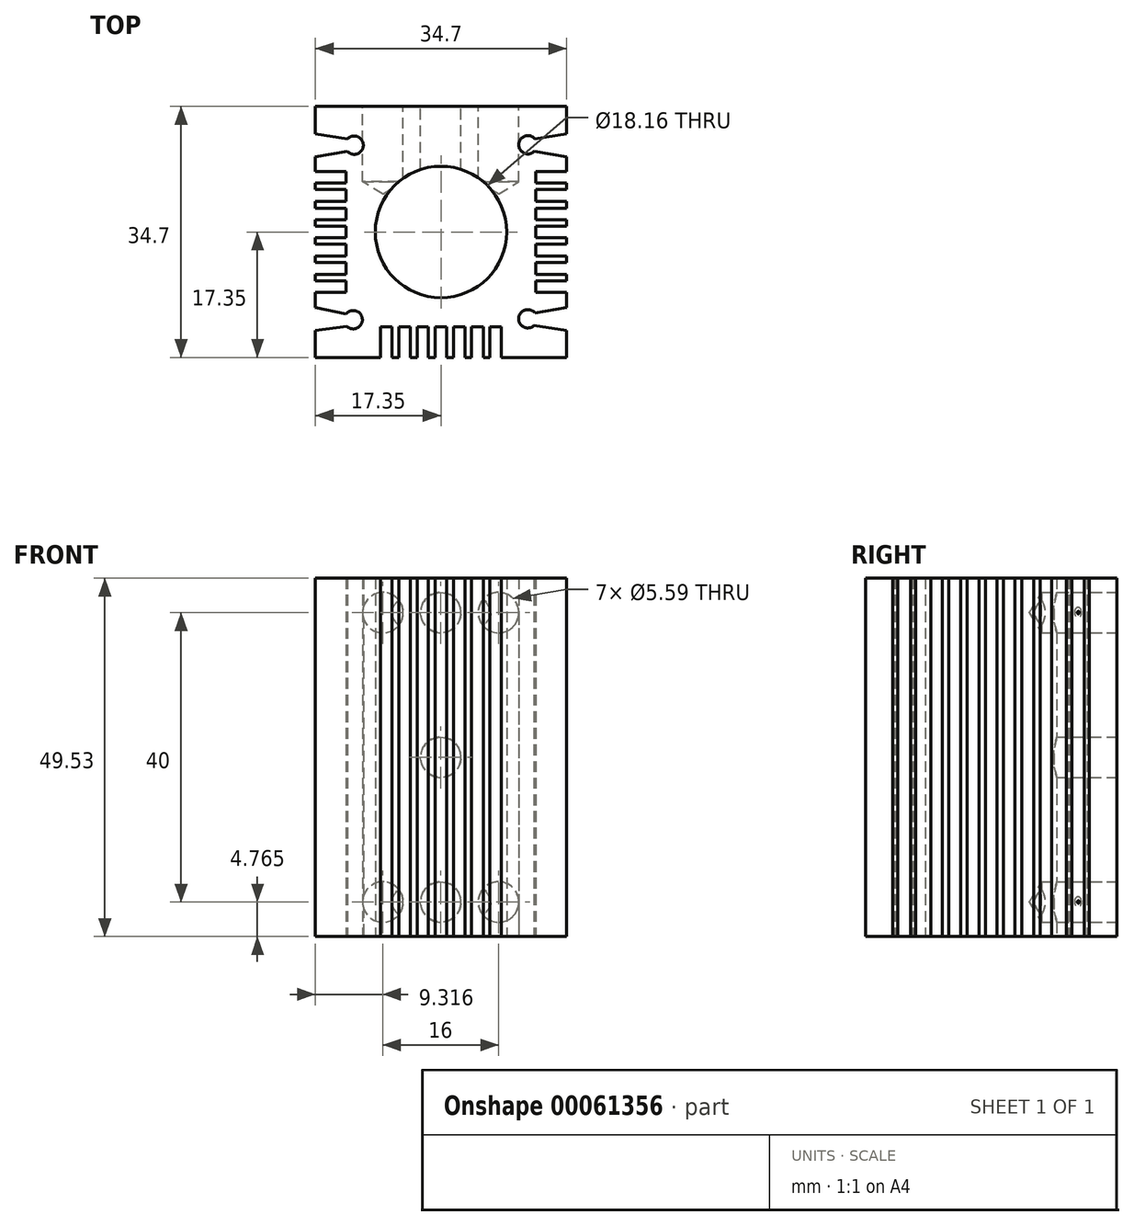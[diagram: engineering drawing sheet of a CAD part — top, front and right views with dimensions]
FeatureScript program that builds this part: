
annotation { "Feature Type Name" : "Feature", "Feature Type Description" : "" }
export const myFeature = defineFeature(function(context is Context, id is Id, definition is map)
    precondition{}
    {
        {
            var Q0;
            Q0=qCreatedBy(makeId("Top.planeOp"),FACE);
            var sketch = newSketch(context, id + "F0", { "sketchPlane" : qUnion([Q0])});
            skLineSegment(sketch, "E0.rect.top", {"start": v(-17.35, -17.35) * mm, "end": v(-8.36, -17.35) * mm});
            skLineSegment(sketch, "E0.rect.left", {"start": v(-17.35, 17.35) * mm, "end": v(-17.35, 13.59) * mm});
            skLineSegment(sketch, "E0.rect.right", {"start": v(17.35, 17.35) * mm, "end": v(17.35, 13.59) * mm});
            skPoint(sketch, "E0.rect.middle", {"position": v(0, 0) * mm});
            skLineSegment(sketch, "E1.rect.left", {"start": v(-6.76, -17.35) * mm, "end": v(-6.76, -13.13) * mm});
            skLineSegment(sketch, "E1.rect.right", {"start": v(6.76, -17.35) * mm, "end": v(6.76, -13.13) * mm});
            skLineSegment(sketch, "E2.rect.left", {"start": v(-5.84, -17.35) * mm, "end": v(-5.84, -13.13) * mm});
            skLineSegment(sketch, "E2.rect.right", {"start": v(5.84, -17.35) * mm, "end": v(5.84, -13.13) * mm});
            skLineSegment(sketch, "E3.trimOffspring", {"start": v(-8.36, -13.13) * mm, "end": v(-8.36, -17.35) * mm});
            skLineSegment(sketch, "E4.trimOffspring", {"start": v(-4.24, -13.13) * mm, "end": v(-4.24, -17.35) * mm});
            skLineSegment(sketch, "E5.trimOffspring", {"start": v(-3.3, -13.13) * mm, "end": v(-3.3, -17.35) * mm});
            skLineSegment(sketch, "E6.trimOffspring", {"start": v(-1.74, -13.13) * mm, "end": v(-1.74, -17.35) * mm});
            skLineSegment(sketch, "E7.trimOffspring", {"start": v(-0.79, -13.13) * mm, "end": v(-0.79, -17.35) * mm});
            skLineSegment(sketch, "E8.trimOffspring", {"start": v(0.79, -13.13) * mm, "end": v(0.79, -17.35) * mm});
            skLineSegment(sketch, "E9.trimOffspring", {"start": v(1.74, -13.13) * mm, "end": v(1.74, -17.35) * mm});
            skLineSegment(sketch, "E10.trimOffspring", {"start": v(3.3, -13.13) * mm, "end": v(3.3, -17.35) * mm});
            skLineSegment(sketch, "E11.trimOffspring", {"start": v(4.24, -13.13) * mm, "end": v(4.24, -17.35) * mm});
            skLineSegment(sketch, "E12.trimOffspring", {"start": v(8.36, -13.13) * mm, "end": v(8.36, -17.35) * mm});
            skLineSegment(sketch, "E13.trimOffspring", {"start": v(-6.76, -17.35) * mm, "end": v(-5.84, -17.35) * mm});
            skLineSegment(sketch, "E14.trimOffspring", {"start": v(-4.24, -17.35) * mm, "end": v(-3.3, -17.35) * mm});
            skLineSegment(sketch, "E15.trimOffspring", {"start": v(-1.74, -17.35) * mm, "end": v(-0.79, -17.35) * mm});
            skLineSegment(sketch, "E16.trimOffspring", {"start": v(0.79, -17.35) * mm, "end": v(1.74, -17.35) * mm});
            skLineSegment(sketch, "E17.trimOffspring", {"start": v(3.3, -17.35) * mm, "end": v(4.24, -17.35) * mm});
            skLineSegment(sketch, "E18.trimOffspring", {"start": v(5.84, -17.35) * mm, "end": v(6.76, -17.35) * mm});
            skLineSegment(sketch, "E19.trimOffspring", {"start": v(8.36, -17.35) * mm, "end": v(17.35, -17.35) * mm});
            skLineSegment(sketch, "E20.trimOffspring", {"start": v(-8.36, -13.13) * mm, "end": v(-6.76, -13.13) * mm});
            skLineSegment(sketch, "E21.trimOffspring", {"start": v(-5.84, -13.13) * mm, "end": v(-4.24, -13.13) * mm});
            skLineSegment(sketch, "E22.trimOffspring", {"start": v(-3.3, -13.13) * mm, "end": v(-1.74, -13.13) * mm});
            skLineSegment(sketch, "E23.trimOffspring", {"start": v(-0.79, -13.13) * mm, "end": v(0.79, -13.13) * mm});
            skLineSegment(sketch, "E24.trimOffspring", {"start": v(1.74, -13.13) * mm, "end": v(3.3, -13.13) * mm});
            skLineSegment(sketch, "E25.trimOffspring", {"start": v(4.24, -13.13) * mm, "end": v(5.84, -13.13) * mm});
            skLineSegment(sketch, "E26.trimOffspring", {"start": v(6.76, -13.13) * mm, "end": v(8.36, -13.13) * mm});
            skPoint(sketch, "E27.rect.right.end.orphan", {"position": v(23.47, -13.13) * mm});
            skPoint(sketch, "E27.rect.left.end.orphan", {"position": v(-23.47, -13.13) * mm});
            skPoint(sketch, "E28.trimOffspring.end.orphan", {"position": v(23.47, 13.13) * mm});
            skPoint(sketch, "E27.rect.bottom.start.orphan", {"position": v(-23.47, 13.13) * mm});
            skLineSegment(sketch, "E29.rect.bottom", {"start": v(-17.35, 5.86) * mm, "end": v(-13.13, 5.86) * mm});
            skLineSegment(sketch, "E29.rect.top", {"start": v(-17.35, -5.86) * mm, "end": v(-13.13, -5.86) * mm});
            skLineSegment(sketch, "E30.rect.bottom", {"start": v(17.35, -6.78) * mm, "end": v(13.13, -6.78) * mm});
            skLineSegment(sketch, "E30.rect.top", {"start": v(17.35, 6.78) * mm, "end": v(13.13, 6.78) * mm});
            skLineSegment(sketch, "E31.rect.bottom", {"start": v(17.35, -8.36) * mm, "end": v(13.13, -8.36) * mm});
            skLineSegment(sketch, "E31.rect.top", {"start": v(17.35, 8.36) * mm, "end": v(13.13, 8.36) * mm});
            skLineSegment(sketch, "E32.rect.left", {"start": v(13.13, 8.36) * mm, "end": v(13.13, 6.78) * mm});
            skLineSegment(sketch, "E33.trimOffspring", {"start": v(-13.13, 8.36) * mm, "end": v(-17.35, 8.36) * mm});
            skLineSegment(sketch, "E34.trimOffspring", {"start": v(-13.13, 6.78) * mm, "end": v(-17.35, 6.78) * mm});
            skLineSegment(sketch, "E35.trimOffspring", {"start": v(13.13, 5.86) * mm, "end": v(17.35, 5.86) * mm});
            skLineSegment(sketch, "E36.trimOffspring", {"start": v(13.13, 4.22) * mm, "end": v(17.35, 4.22) * mm});
            skLineSegment(sketch, "E37.trimOffspring", {"start": v(13.13, 3.3) * mm, "end": v(17.35, 3.3) * mm});
            skLineSegment(sketch, "E38.trimOffspring", {"start": v(13.13, 1.68) * mm, "end": v(17.35, 1.68) * mm});
            skLineSegment(sketch, "E39.trimOffspring", {"start": v(13.13, 0.79) * mm, "end": v(17.35, 0.79) * mm});
            skLineSegment(sketch, "E40.trimOffspring", {"start": v(13.13, -0.79) * mm, "end": v(17.35, -0.79) * mm});
            skLineSegment(sketch, "E41.trimOffspring", {"start": v(13.13, -1.68) * mm, "end": v(17.35, -1.68) * mm});
            skLineSegment(sketch, "E42.trimOffspring", {"start": v(13.13, -3.3) * mm, "end": v(17.35, -3.3) * mm});
            skLineSegment(sketch, "E43.trimOffspring", {"start": v(13.13, -4.22) * mm, "end": v(17.35, -4.22) * mm});
            skLineSegment(sketch, "E44.trimOffspring", {"start": v(13.13, -5.86) * mm, "end": v(17.35, -5.86) * mm});
            skLineSegment(sketch, "E45.trimOffspring", {"start": v(-13.13, -6.78) * mm, "end": v(-17.35, -6.78) * mm});
            skLineSegment(sketch, "E46.trimOffspring", {"start": v(-13.13, -8.36) * mm, "end": v(-17.35, -8.36) * mm});
            skLineSegment(sketch, "E47.trimOffspring", {"start": v(-17.35, 4.22) * mm, "end": v(-13.13, 4.22) * mm});
            skLineSegment(sketch, "E48.trimOffspring", {"start": v(-17.35, 3.3) * mm, "end": v(-13.13, 3.3) * mm});
            skLineSegment(sketch, "E49.trimOffspring", {"start": v(-17.35, 1.68) * mm, "end": v(-13.13, 1.68) * mm});
            skLineSegment(sketch, "E50.trimOffspring", {"start": v(-17.35, 0.79) * mm, "end": v(-13.13, 0.79) * mm});
            skLineSegment(sketch, "E51.trimOffspring", {"start": v(-17.35, -0.79) * mm, "end": v(-13.13, -0.79) * mm});
            skLineSegment(sketch, "E52.trimOffspring", {"start": v(-17.35, -1.68) * mm, "end": v(-13.13, -1.68) * mm});
            skLineSegment(sketch, "E53.trimOffspring", {"start": v(-17.35, -3.3) * mm, "end": v(-13.13, -3.3) * mm});
            skLineSegment(sketch, "E54.trimOffspring", {"start": v(-17.35, -4.22) * mm, "end": v(-13.13, -4.22) * mm});
            skPoint(sketch, "E32.rect.top.end.orphan", {"position": v(-13.13, -20.84) * mm});
            skPoint(sketch, "E32.rect.top.start.orphan", {"position": v(13.13, -20.84) * mm});
            skPoint(sketch, "E55.orphan", {"position": v(13.13, 20.84) * mm});
            skLineSegment(sketch, "E56.trimOffspring", {"start": v(-13.13, 8.36) * mm, "end": v(-13.13, 6.78) * mm});
            skPoint(sketch, "E32.rect.right.start.orphan", {"position": v(-13.13, 20.84) * mm});
            skLineSegment(sketch, "E57.trimOffspring", {"start": v(-17.35, -8.36) * mm, "end": v(-17.35, -10.46) * mm});
            skLineSegment(sketch, "E58.trimOffspring", {"start": v(-17.35, -5.86) * mm, "end": v(-17.35, -6.78) * mm});
            skLineSegment(sketch, "E59.trimOffspring", {"start": v(-17.35, -3.3) * mm, "end": v(-17.35, -4.22) * mm});
            skLineSegment(sketch, "E60.trimOffspring", {"start": v(-17.35, -0.79) * mm, "end": v(-17.35, -1.68) * mm});
            skLineSegment(sketch, "E61.trimOffspring", {"start": v(-17.35, 1.68) * mm, "end": v(-17.35, 0.79) * mm});
            skLineSegment(sketch, "E62.trimOffspring", {"start": v(-17.35, 4.22) * mm, "end": v(-17.35, 3.3) * mm});
            skLineSegment(sketch, "E63.trimOffspring", {"start": v(-17.35, 6.78) * mm, "end": v(-17.35, 5.86) * mm});
            skLineSegment(sketch, "E64.trimOffspring", {"start": v(-13.13, 5.86) * mm, "end": v(-13.13, 4.22) * mm});
            skLineSegment(sketch, "E65.trimOffspring", {"start": v(-13.13, 3.3) * mm, "end": v(-13.13, 1.68) * mm});
            skLineSegment(sketch, "E66.trimOffspring", {"start": v(-13.13, 0.79) * mm, "end": v(-13.13, -0.79) * mm});
            skLineSegment(sketch, "E67.trimOffspring", {"start": v(-13.13, -1.68) * mm, "end": v(-13.13, -3.3) * mm});
            skLineSegment(sketch, "E68.trimOffspring", {"start": v(-13.13, -4.22) * mm, "end": v(-13.13, -5.86) * mm});
            skLineSegment(sketch, "E69.trimOffspring", {"start": v(-13.13, -6.78) * mm, "end": v(-13.13, -8.36) * mm});
            skLineSegment(sketch, "E70", {"start": v(13.13, -8.36) * mm, "end": v(13.13, -6.78) * mm});
            skLineSegment(sketch, "E71.trimOffspring", {"start": v(17.35, -8.36) * mm, "end": v(17.35, -10.46) * mm});
            skLineSegment(sketch, "E72.trimOffspring", {"start": v(17.35, -5.86) * mm, "end": v(17.35, -6.78) * mm});
            skLineSegment(sketch, "E73.trimOffspring", {"start": v(17.35, -3.3) * mm, "end": v(17.35, -4.22) * mm});
            skLineSegment(sketch, "E74.trimOffspring", {"start": v(17.35, -0.79) * mm, "end": v(17.35, -1.68) * mm});
            skLineSegment(sketch, "E75.trimOffspring", {"start": v(17.35, 1.68) * mm, "end": v(17.35, 0.79) * mm});
            skLineSegment(sketch, "E76.trimOffspring", {"start": v(17.35, 4.22) * mm, "end": v(17.35, 3.3) * mm});
            skLineSegment(sketch, "E77.trimOffspring", {"start": v(17.35, 6.78) * mm, "end": v(17.35, 5.86) * mm});
            skLineSegment(sketch, "E78.trimOffspring", {"start": v(13.13, 5.86) * mm, "end": v(13.13, 4.22) * mm});
            skLineSegment(sketch, "E79.trimOffspring", {"start": v(13.13, 3.3) * mm, "end": v(13.13, 1.68) * mm});
            skLineSegment(sketch, "E80.trimOffspring", {"start": v(13.13, 0.79) * mm, "end": v(13.13, -0.79) * mm});
            skLineSegment(sketch, "E81.trimOffspring", {"start": v(13.13, -1.68) * mm, "end": v(13.13, -3.3) * mm});
            skLineSegment(sketch, "E82.trimOffspring", {"start": v(13.13, -4.22) * mm, "end": v(13.13, -5.86) * mm});
            skLineSegment(sketch, "E83", {"start": v(-17.35, 17.35) * mm, "end": v(17.35, 17.35) * mm});
            skPoint(sketch, "E84", {"position": v(-12, 12) * mm});
            skPoint(sketch, "E85", {"position": v(12.13, 12.13) * mm});
            skPoint(sketch, "E86", {"position": v(12, -12) * mm});
            skPoint(sketch, "E87", {"position": v(-12.13, -12.13) * mm});
            skArc(sketch, "E88", {"start": v(-12.92, 11.13) * mm, "mid": v(-10.73, 12) * mm, "end": v(-12.92, 12.88) * mm});
            skArc(sketch, "E89", {"start": v(13, 12.88) * mm, "mid": v(10.76, 12.13) * mm, "end": v(12.89, 11.13) * mm});
            skPoint(sketch, "E90.rect.middle", {"position": v(0, 12) * mm});
            skLineSegment(sketch, "E91", {"start": v(13, 12.88) * mm, "end": v(17.35, 13.59) * mm});
            skLineSegment(sketch, "E92", {"start": v(12.89, 11.13) * mm, "end": v(17.35, 10.41) * mm});
            skLineSegment(sketch, "E93", {"start": v(-17.35, 13.59) * mm, "end": v(-12.92, 12.88) * mm});
            skLineSegment(sketch, "E94", {"start": v(-17.35, 10.41) * mm, "end": v(-12.92, 11.13) * mm});
            skLineSegment(sketch, "E95.trimOffspring", {"start": v(-17.35, 10.41) * mm, "end": v(-17.35, 8.36) * mm});
            skLineSegment(sketch, "E96.trimOffspring", {"start": v(17.35, 10.41) * mm, "end": v(17.35, 8.36) * mm});
            skPoint(sketch, "E97.orphan", {"position": v(0, -12.05) * mm});
            skArc(sketch, "E98", {"start": v(-13, -13.05) * mm, "mid": v(-10.86, -12.06) * mm, "end": v(-13.1, -11.3) * mm});
            skArc(sketch, "E99", {"start": v(12.96, -11.17) * mm, "mid": v(10.73, -11.94) * mm, "end": v(12.87, -12.92) * mm});
            skLineSegment(sketch, "E100", {"start": v(-13.1, -11.3) * mm, "end": v(-17.35, -10.46) * mm});
            skLineSegment(sketch, "E101", {"start": v(-13, -13.05) * mm, "end": v(-17.35, -13.64) * mm});
            skLineSegment(sketch, "E102", {"start": v(12.96, -11.17) * mm, "end": v(17.35, -10.46) * mm});
            skLineSegment(sketch, "E103", {"start": v(12.87, -12.92) * mm, "end": v(17.35, -13.64) * mm});
            skLineSegment(sketch, "E104.trimOffspring", {"start": v(17.35, -13.64) * mm, "end": v(17.35, -17.35) * mm});
            skLineSegment(sketch, "E105.trimOffspring", {"start": v(-17.35, -13.64) * mm, "end": v(-17.35, -17.35) * mm});
            skSolve(sketch);
        }
        {
            var Q0;
            Q0 = qSketchRegion(id + "F0", true);
            extrude(context, id + "F1", {"entities" : qUnion([Q0]), "depth" : 49.53 * mm});
        }
        {
            var Q0;
            Q0=sQuery(id+"F0.wireOp",VERTEX,"E0.rect.middle");
            var Q1;
            Q1=makeQuery(id+"F1.opExtrude","SWEPT_BODY",BODY,{"disambiguationData":[OSD([sQuery(id+"F0.wireOp",EDGE,"E0.rect.top"),sQuery(id+"F0.wireOp",EDGE,"E0.rect.left"),sQuery(id+"F0.wireOp",EDGE,"E0.rect.right"),sQuery(id+"F0.wireOp",EDGE,"E1.rect.left"),sQuery(id+"F0.wireOp",EDGE,"E1.rect.right"),sQuery(id+"F0.wireOp",EDGE,"E2.rect.left"),sQuery(id+"F0.wireOp",EDGE,"E2.rect.right"),sQuery(id+"F0.wireOp",EDGE,"E3.trimOffspring"),sQuery(id+"F0.wireOp",EDGE,"E4.trimOffspring"),sQuery(id+"F0.wireOp",EDGE,"E5.trimOffspring"),sQuery(id+"F0.wireOp",EDGE,"E6.trimOffspring"),sQuery(id+"F0.wireOp",EDGE,"E7.trimOffspring"),sQuery(id+"F0.wireOp",EDGE,"E8.trimOffspring"),sQuery(id+"F0.wireOp",EDGE,"E9.trimOffspring"),sQuery(id+"F0.wireOp",EDGE,"E10.trimOffspring"),sQuery(id+"F0.wireOp",EDGE,"E11.trimOffspring"),sQuery(id+"F0.wireOp",EDGE,"E12.trimOffspring"),sQuery(id+"F0.wireOp",EDGE,"E13.trimOffspring"),sQuery(id+"F0.wireOp",EDGE,"E14.trimOffspring"),sQuery(id+"F0.wireOp",EDGE,"E15.trimOffspring"),sQuery(id+"F0.wireOp",EDGE,"E16.trimOffspring"),sQuery(id+"F0.wireOp",EDGE,"E17.trimOffspring"),sQuery(id+"F0.wireOp",EDGE,"E18.trimOffspring"),sQuery(id+"F0.wireOp",EDGE,"E19.trimOffspring"),sQuery(id+"F0.wireOp",EDGE,"E20.trimOffspring"),sQuery(id+"F0.wireOp",EDGE,"E21.trimOffspring"),sQuery(id+"F0.wireOp",EDGE,"E22.trimOffspring"),sQuery(id+"F0.wireOp",EDGE,"E23.trimOffspring"),sQuery(id+"F0.wireOp",EDGE,"E24.trimOffspring"),sQuery(id+"F0.wireOp",EDGE,"E25.trimOffspring"),sQuery(id+"F0.wireOp",EDGE,"E26.trimOffspring"),sQuery(id+"F0.wireOp",EDGE,"E29.rect.bottom"),sQuery(id+"F0.wireOp",EDGE,"E29.rect.top"),sQuery(id+"F0.wireOp",EDGE,"E30.rect.bottom"),sQuery(id+"F0.wireOp",EDGE,"E30.rect.top"),sQuery(id+"F0.wireOp",EDGE,"E31.rect.bottom"),sQuery(id+"F0.wireOp",EDGE,"E31.rect.top"),sQuery(id+"F0.wireOp",EDGE,"E32.rect.left"),sQuery(id+"F0.wireOp",EDGE,"E33.trimOffspring"),sQuery(id+"F0.wireOp",EDGE,"E34.trimOffspring"),sQuery(id+"F0.wireOp",EDGE,"E35.trimOffspring"),sQuery(id+"F0.wireOp",EDGE,"E36.trimOffspring"),sQuery(id+"F0.wireOp",EDGE,"E37.trimOffspring"),sQuery(id+"F0.wireOp",EDGE,"E38.trimOffspring"),sQuery(id+"F0.wireOp",EDGE,"E39.trimOffspring"),sQuery(id+"F0.wireOp",EDGE,"E40.trimOffspring"),sQuery(id+"F0.wireOp",EDGE,"E41.trimOffspring"),sQuery(id+"F0.wireOp",EDGE,"E42.trimOffspring"),sQuery(id+"F0.wireOp",EDGE,"E43.trimOffspring"),sQuery(id+"F0.wireOp",EDGE,"E44.trimOffspring"),sQuery(id+"F0.wireOp",EDGE,"E45.trimOffspring"),sQuery(id+"F0.wireOp",EDGE,"E46.trimOffspring"),sQuery(id+"F0.wireOp",EDGE,"E47.trimOffspring"),sQuery(id+"F0.wireOp",EDGE,"E48.trimOffspring"),sQuery(id+"F0.wireOp",EDGE,"E49.trimOffspring"),sQuery(id+"F0.wireOp",EDGE,"E50.trimOffspring"),sQuery(id+"F0.wireOp",EDGE,"E51.trimOffspring"),sQuery(id+"F0.wireOp",EDGE,"E52.trimOffspring"),sQuery(id+"F0.wireOp",EDGE,"E53.trimOffspring"),sQuery(id+"F0.wireOp",EDGE,"E54.trimOffspring"),sQuery(id+"F0.wireOp",EDGE,"E56.trimOffspring"),sQuery(id+"F0.wireOp",EDGE,"E57.trimOffspring"),sQuery(id+"F0.wireOp",EDGE,"E58.trimOffspring"),sQuery(id+"F0.wireOp",EDGE,"E59.trimOffspring"),sQuery(id+"F0.wireOp",EDGE,"E60.trimOffspring"),sQuery(id+"F0.wireOp",EDGE,"E61.trimOffspring"),sQuery(id+"F0.wireOp",EDGE,"E62.trimOffspring"),sQuery(id+"F0.wireOp",EDGE,"E63.trimOffspring"),sQuery(id+"F0.wireOp",EDGE,"E64.trimOffspring"),sQuery(id+"F0.wireOp",EDGE,"E65.trimOffspring"),sQuery(id+"F0.wireOp",EDGE,"E66.trimOffspring"),sQuery(id+"F0.wireOp",EDGE,"E67.trimOffspring"),sQuery(id+"F0.wireOp",EDGE,"E68.trimOffspring"),sQuery(id+"F0.wireOp",EDGE,"E69.trimOffspring"),sQuery(id+"F0.wireOp",EDGE,"E70"),sQuery(id+"F0.wireOp",EDGE,"E71.trimOffspring"),sQuery(id+"F0.wireOp",EDGE,"E72.trimOffspring"),sQuery(id+"F0.wireOp",EDGE,"E73.trimOffspring"),sQuery(id+"F0.wireOp",EDGE,"E74.trimOffspring"),sQuery(id+"F0.wireOp",EDGE,"E75.trimOffspring"),sQuery(id+"F0.wireOp",EDGE,"E76.trimOffspring"),sQuery(id+"F0.wireOp",EDGE,"E77.trimOffspring"),sQuery(id+"F0.wireOp",EDGE,"E78.trimOffspring"),sQuery(id+"F0.wireOp",EDGE,"E79.trimOffspring"),sQuery(id+"F0.wireOp",EDGE,"E80.trimOffspring"),sQuery(id+"F0.wireOp",EDGE,"E81.trimOffspring"),sQuery(id+"F0.wireOp",EDGE,"E82.trimOffspring"),sQuery(id+"F0.wireOp",EDGE,"E83"),sQuery(id+"F0.wireOp",EDGE,"E88"),sQuery(id+"F0.wireOp",EDGE,"E89"),sQuery(id+"F0.wireOp",EDGE,"E91"),sQuery(id+"F0.wireOp",EDGE,"E92"),sQuery(id+"F0.wireOp",EDGE,"E93"),sQuery(id+"F0.wireOp",EDGE,"E94"),sQuery(id+"F0.wireOp",EDGE,"E95.trimOffspring"),sQuery(id+"F0.wireOp",EDGE,"E96.trimOffspring"),sQuery(id+"F0.wireOp",EDGE,"E98"),sQuery(id+"F0.wireOp",EDGE,"E99"),sQuery(id+"F0.wireOp",EDGE,"E100"),sQuery(id+"F0.wireOp",EDGE,"E101"),sQuery(id+"F0.wireOp",EDGE,"E102"),sQuery(id+"F0.wireOp",EDGE,"E103"),sQuery(id+"F0.wireOp",EDGE,"E104.trimOffspring"),sQuery(id+"F0.wireOp",EDGE,"E105.trimOffspring")])]});
            hole(context, id + "F2", {"style" : HoleStyle.SIMPLE, "holeDiameter" : 18.16 * mm, "endStyle" : HoleEndStyle.THROUGH, "oppositeDirection" : true, "locations" : qUnion([Q0]), "scope" : qUnion([Q1])});
        }
        {
            var Q0;
            Q0=makeQuery(id+"F1.opExtrude","SWEPT_FACE",FACE,{"disambiguationData":[OSD([sQuery(id+"F0.wireOp",EDGE,"E83")])]});
            var sketch = newSketch(context, id + "F3", { "sketchPlane" : qUnion([Q0])});
            skLineSegment(sketch, "E106.bottom", {"start": v(17.35, 49.53) * mm, "end": v(-17.35, 49.53) * mm});
            skLineSegment(sketch, "E106.top", {"start": v(17.35, 0) * mm, "end": v(-17.35, 0) * mm});
            skLineSegment(sketch, "E106.left", {"start": v(17.35, 49.53) * mm, "end": v(17.35, 0) * mm});
            skLineSegment(sketch, "E106.right", {"start": v(-17.35, 49.53) * mm, "end": v(-17.35, 0) * mm});
            skPoint(sketch, "E107", {"position": v(0.03, 24.77) * mm});
            skLineSegment(sketch, "E108.rect.bottom", {"start": v(8.03, 44.77) * mm, "end": v(-7.97, 44.77) * mm});
            skLineSegment(sketch, "E108.rect.top", {"start": v(8.03, 4.76) * mm, "end": v(-7.97, 4.76) * mm});
            skLineSegment(sketch, "E108.rect.left", {"start": v(8.03, 44.77) * mm, "end": v(8.03, 4.76) * mm});
            skLineSegment(sketch, "E108.rect.right", {"start": v(-7.97, 44.77) * mm, "end": v(-7.97, 4.76) * mm});
            skPoint(sketch, "E109", {"position": v(8.03, 44.77) * mm});
            skPoint(sketch, "E110", {"position": v(8.03, 4.76) * mm});
            skPoint(sketch, "E111", {"position": v(-7.97, 4.76) * mm});
            skPoint(sketch, "E112", {"position": v(-7.97, 44.77) * mm});
            skPoint(sketch, "E113", {"position": v(0.03, 44.77) * mm});
            skPoint(sketch, "E114", {"position": v(0.03, 4.76) * mm});
            skSolve(sketch);
        }
        {
            var Q0;
            Q0=sQuery(id+"F3.wireOp",VERTEX,"E113");
            var Q1;
            Q1=sQuery(id+"F3.wireOp",VERTEX,"E114");
            var Q2;
            Q2=makeQuery(id+"F1.opExtrude","SWEPT_BODY",BODY,{"disambiguationData":[OSD([sQuery(id+"F0.wireOp",EDGE,"E0.rect.top"),sQuery(id+"F0.wireOp",EDGE,"E0.rect.left"),sQuery(id+"F0.wireOp",EDGE,"E0.rect.right"),sQuery(id+"F0.wireOp",EDGE,"E1.rect.left"),sQuery(id+"F0.wireOp",EDGE,"E1.rect.right"),sQuery(id+"F0.wireOp",EDGE,"E2.rect.left"),sQuery(id+"F0.wireOp",EDGE,"E2.rect.right"),sQuery(id+"F0.wireOp",EDGE,"E3.trimOffspring"),sQuery(id+"F0.wireOp",EDGE,"E4.trimOffspring"),sQuery(id+"F0.wireOp",EDGE,"E5.trimOffspring"),sQuery(id+"F0.wireOp",EDGE,"E6.trimOffspring"),sQuery(id+"F0.wireOp",EDGE,"E7.trimOffspring"),sQuery(id+"F0.wireOp",EDGE,"E8.trimOffspring"),sQuery(id+"F0.wireOp",EDGE,"E9.trimOffspring"),sQuery(id+"F0.wireOp",EDGE,"E10.trimOffspring"),sQuery(id+"F0.wireOp",EDGE,"E11.trimOffspring"),sQuery(id+"F0.wireOp",EDGE,"E12.trimOffspring"),sQuery(id+"F0.wireOp",EDGE,"E13.trimOffspring"),sQuery(id+"F0.wireOp",EDGE,"E14.trimOffspring"),sQuery(id+"F0.wireOp",EDGE,"E15.trimOffspring"),sQuery(id+"F0.wireOp",EDGE,"E16.trimOffspring"),sQuery(id+"F0.wireOp",EDGE,"E17.trimOffspring"),sQuery(id+"F0.wireOp",EDGE,"E18.trimOffspring"),sQuery(id+"F0.wireOp",EDGE,"E19.trimOffspring"),sQuery(id+"F0.wireOp",EDGE,"E20.trimOffspring"),sQuery(id+"F0.wireOp",EDGE,"E21.trimOffspring"),sQuery(id+"F0.wireOp",EDGE,"E22.trimOffspring"),sQuery(id+"F0.wireOp",EDGE,"E23.trimOffspring"),sQuery(id+"F0.wireOp",EDGE,"E24.trimOffspring"),sQuery(id+"F0.wireOp",EDGE,"E25.trimOffspring"),sQuery(id+"F0.wireOp",EDGE,"E26.trimOffspring"),sQuery(id+"F0.wireOp",EDGE,"E29.rect.bottom"),sQuery(id+"F0.wireOp",EDGE,"E29.rect.top"),sQuery(id+"F0.wireOp",EDGE,"E30.rect.bottom"),sQuery(id+"F0.wireOp",EDGE,"E30.rect.top"),sQuery(id+"F0.wireOp",EDGE,"E31.rect.bottom"),sQuery(id+"F0.wireOp",EDGE,"E31.rect.top"),sQuery(id+"F0.wireOp",EDGE,"E32.rect.left"),sQuery(id+"F0.wireOp",EDGE,"E33.trimOffspring"),sQuery(id+"F0.wireOp",EDGE,"E34.trimOffspring"),sQuery(id+"F0.wireOp",EDGE,"E35.trimOffspring"),sQuery(id+"F0.wireOp",EDGE,"E36.trimOffspring"),sQuery(id+"F0.wireOp",EDGE,"E37.trimOffspring"),sQuery(id+"F0.wireOp",EDGE,"E38.trimOffspring"),sQuery(id+"F0.wireOp",EDGE,"E39.trimOffspring"),sQuery(id+"F0.wireOp",EDGE,"E40.trimOffspring"),sQuery(id+"F0.wireOp",EDGE,"E41.trimOffspring"),sQuery(id+"F0.wireOp",EDGE,"E42.trimOffspring"),sQuery(id+"F0.wireOp",EDGE,"E43.trimOffspring"),sQuery(id+"F0.wireOp",EDGE,"E44.trimOffspring"),sQuery(id+"F0.wireOp",EDGE,"E45.trimOffspring"),sQuery(id+"F0.wireOp",EDGE,"E46.trimOffspring"),sQuery(id+"F0.wireOp",EDGE,"E47.trimOffspring"),sQuery(id+"F0.wireOp",EDGE,"E48.trimOffspring"),sQuery(id+"F0.wireOp",EDGE,"E49.trimOffspring"),sQuery(id+"F0.wireOp",EDGE,"E50.trimOffspring"),sQuery(id+"F0.wireOp",EDGE,"E51.trimOffspring"),sQuery(id+"F0.wireOp",EDGE,"E52.trimOffspring"),sQuery(id+"F0.wireOp",EDGE,"E53.trimOffspring"),sQuery(id+"F0.wireOp",EDGE,"E54.trimOffspring"),sQuery(id+"F0.wireOp",EDGE,"E56.trimOffspring"),sQuery(id+"F0.wireOp",EDGE,"E57.trimOffspring"),sQuery(id+"F0.wireOp",EDGE,"E58.trimOffspring"),sQuery(id+"F0.wireOp",EDGE,"E59.trimOffspring"),sQuery(id+"F0.wireOp",EDGE,"E60.trimOffspring"),sQuery(id+"F0.wireOp",EDGE,"E61.trimOffspring"),sQuery(id+"F0.wireOp",EDGE,"E62.trimOffspring"),sQuery(id+"F0.wireOp",EDGE,"E63.trimOffspring"),sQuery(id+"F0.wireOp",EDGE,"E64.trimOffspring"),sQuery(id+"F0.wireOp",EDGE,"E65.trimOffspring"),sQuery(id+"F0.wireOp",EDGE,"E66.trimOffspring"),sQuery(id+"F0.wireOp",EDGE,"E67.trimOffspring"),sQuery(id+"F0.wireOp",EDGE,"E68.trimOffspring"),sQuery(id+"F0.wireOp",EDGE,"E69.trimOffspring"),sQuery(id+"F0.wireOp",EDGE,"E70"),sQuery(id+"F0.wireOp",EDGE,"E71.trimOffspring"),sQuery(id+"F0.wireOp",EDGE,"E72.trimOffspring"),sQuery(id+"F0.wireOp",EDGE,"E73.trimOffspring"),sQuery(id+"F0.wireOp",EDGE,"E74.trimOffspring"),sQuery(id+"F0.wireOp",EDGE,"E75.trimOffspring"),sQuery(id+"F0.wireOp",EDGE,"E76.trimOffspring"),sQuery(id+"F0.wireOp",EDGE,"E77.trimOffspring"),sQuery(id+"F0.wireOp",EDGE,"E78.trimOffspring"),sQuery(id+"F0.wireOp",EDGE,"E79.trimOffspring"),sQuery(id+"F0.wireOp",EDGE,"E80.trimOffspring"),sQuery(id+"F0.wireOp",EDGE,"E81.trimOffspring"),sQuery(id+"F0.wireOp",EDGE,"E82.trimOffspring"),sQuery(id+"F0.wireOp",EDGE,"E83"),sQuery(id+"F0.wireOp",EDGE,"E88"),sQuery(id+"F0.wireOp",EDGE,"E89"),sQuery(id+"F0.wireOp",EDGE,"E91"),sQuery(id+"F0.wireOp",EDGE,"E92"),sQuery(id+"F0.wireOp",EDGE,"E93"),sQuery(id+"F0.wireOp",EDGE,"E94"),sQuery(id+"F0.wireOp",EDGE,"E95.trimOffspring"),sQuery(id+"F0.wireOp",EDGE,"E96.trimOffspring"),sQuery(id+"F0.wireOp",EDGE,"E98"),sQuery(id+"F0.wireOp",EDGE,"E99"),sQuery(id+"F0.wireOp",EDGE,"E100"),sQuery(id+"F0.wireOp",EDGE,"E101"),sQuery(id+"F0.wireOp",EDGE,"E102"),sQuery(id+"F0.wireOp",EDGE,"E103"),sQuery(id+"F0.wireOp",EDGE,"E104.trimOffspring"),sQuery(id+"F0.wireOp",EDGE,"E105.trimOffspring")])]});
            hole(context, id + "F4", {"style" : HoleStyle.SIMPLE, "holeDiameter" : 3 * mm, "endStyle" : HoleEndStyle.BLIND, "holeDepth" : 7.37 * mm, "locations" : qUnion([Q0, Q1]), "scope" : qUnion([Q2])});
        }
        {
            var Q0;
            Q0=sQuery(id+"F3.wireOp",VERTEX,"E109");
            var Q1;
            Q1=sQuery(id+"F3.wireOp",VERTEX,"E110");
            var Q2;
            Q2=sQuery(id+"F3.wireOp",VERTEX,"E111");
            var Q3;
            Q3=sQuery(id+"F3.wireOp",VERTEX,"E112");
            var Q4;
            Q4=makeQuery(id+"F1.opExtrude","SWEPT_BODY",BODY,{"disambiguationData":[OSD([sQuery(id+"F0.wireOp",EDGE,"E0.rect.top"),sQuery(id+"F0.wireOp",EDGE,"E0.rect.left"),sQuery(id+"F0.wireOp",EDGE,"E0.rect.right"),sQuery(id+"F0.wireOp",EDGE,"E1.rect.left"),sQuery(id+"F0.wireOp",EDGE,"E1.rect.right"),sQuery(id+"F0.wireOp",EDGE,"E2.rect.left"),sQuery(id+"F0.wireOp",EDGE,"E2.rect.right"),sQuery(id+"F0.wireOp",EDGE,"E3.trimOffspring"),sQuery(id+"F0.wireOp",EDGE,"E4.trimOffspring"),sQuery(id+"F0.wireOp",EDGE,"E5.trimOffspring"),sQuery(id+"F0.wireOp",EDGE,"E6.trimOffspring"),sQuery(id+"F0.wireOp",EDGE,"E7.trimOffspring"),sQuery(id+"F0.wireOp",EDGE,"E8.trimOffspring"),sQuery(id+"F0.wireOp",EDGE,"E9.trimOffspring"),sQuery(id+"F0.wireOp",EDGE,"E10.trimOffspring"),sQuery(id+"F0.wireOp",EDGE,"E11.trimOffspring"),sQuery(id+"F0.wireOp",EDGE,"E12.trimOffspring"),sQuery(id+"F0.wireOp",EDGE,"E13.trimOffspring"),sQuery(id+"F0.wireOp",EDGE,"E14.trimOffspring"),sQuery(id+"F0.wireOp",EDGE,"E15.trimOffspring"),sQuery(id+"F0.wireOp",EDGE,"E16.trimOffspring"),sQuery(id+"F0.wireOp",EDGE,"E17.trimOffspring"),sQuery(id+"F0.wireOp",EDGE,"E18.trimOffspring"),sQuery(id+"F0.wireOp",EDGE,"E19.trimOffspring"),sQuery(id+"F0.wireOp",EDGE,"E20.trimOffspring"),sQuery(id+"F0.wireOp",EDGE,"E21.trimOffspring"),sQuery(id+"F0.wireOp",EDGE,"E22.trimOffspring"),sQuery(id+"F0.wireOp",EDGE,"E23.trimOffspring"),sQuery(id+"F0.wireOp",EDGE,"E24.trimOffspring"),sQuery(id+"F0.wireOp",EDGE,"E25.trimOffspring"),sQuery(id+"F0.wireOp",EDGE,"E26.trimOffspring"),sQuery(id+"F0.wireOp",EDGE,"E29.rect.bottom"),sQuery(id+"F0.wireOp",EDGE,"E29.rect.top"),sQuery(id+"F0.wireOp",EDGE,"E30.rect.bottom"),sQuery(id+"F0.wireOp",EDGE,"E30.rect.top"),sQuery(id+"F0.wireOp",EDGE,"E31.rect.bottom"),sQuery(id+"F0.wireOp",EDGE,"E31.rect.top"),sQuery(id+"F0.wireOp",EDGE,"E32.rect.left"),sQuery(id+"F0.wireOp",EDGE,"E33.trimOffspring"),sQuery(id+"F0.wireOp",EDGE,"E34.trimOffspring"),sQuery(id+"F0.wireOp",EDGE,"E35.trimOffspring"),sQuery(id+"F0.wireOp",EDGE,"E36.trimOffspring"),sQuery(id+"F0.wireOp",EDGE,"E37.trimOffspring"),sQuery(id+"F0.wireOp",EDGE,"E38.trimOffspring"),sQuery(id+"F0.wireOp",EDGE,"E39.trimOffspring"),sQuery(id+"F0.wireOp",EDGE,"E40.trimOffspring"),sQuery(id+"F0.wireOp",EDGE,"E41.trimOffspring"),sQuery(id+"F0.wireOp",EDGE,"E42.trimOffspring"),sQuery(id+"F0.wireOp",EDGE,"E43.trimOffspring"),sQuery(id+"F0.wireOp",EDGE,"E44.trimOffspring"),sQuery(id+"F0.wireOp",EDGE,"E45.trimOffspring"),sQuery(id+"F0.wireOp",EDGE,"E46.trimOffspring"),sQuery(id+"F0.wireOp",EDGE,"E47.trimOffspring"),sQuery(id+"F0.wireOp",EDGE,"E48.trimOffspring"),sQuery(id+"F0.wireOp",EDGE,"E49.trimOffspring"),sQuery(id+"F0.wireOp",EDGE,"E50.trimOffspring"),sQuery(id+"F0.wireOp",EDGE,"E51.trimOffspring"),sQuery(id+"F0.wireOp",EDGE,"E52.trimOffspring"),sQuery(id+"F0.wireOp",EDGE,"E53.trimOffspring"),sQuery(id+"F0.wireOp",EDGE,"E54.trimOffspring"),sQuery(id+"F0.wireOp",EDGE,"E56.trimOffspring"),sQuery(id+"F0.wireOp",EDGE,"E57.trimOffspring"),sQuery(id+"F0.wireOp",EDGE,"E58.trimOffspring"),sQuery(id+"F0.wireOp",EDGE,"E59.trimOffspring"),sQuery(id+"F0.wireOp",EDGE,"E60.trimOffspring"),sQuery(id+"F0.wireOp",EDGE,"E61.trimOffspring"),sQuery(id+"F0.wireOp",EDGE,"E62.trimOffspring"),sQuery(id+"F0.wireOp",EDGE,"E63.trimOffspring"),sQuery(id+"F0.wireOp",EDGE,"E64.trimOffspring"),sQuery(id+"F0.wireOp",EDGE,"E65.trimOffspring"),sQuery(id+"F0.wireOp",EDGE,"E66.trimOffspring"),sQuery(id+"F0.wireOp",EDGE,"E67.trimOffspring"),sQuery(id+"F0.wireOp",EDGE,"E68.trimOffspring"),sQuery(id+"F0.wireOp",EDGE,"E69.trimOffspring"),sQuery(id+"F0.wireOp",EDGE,"E70"),sQuery(id+"F0.wireOp",EDGE,"E71.trimOffspring"),sQuery(id+"F0.wireOp",EDGE,"E72.trimOffspring"),sQuery(id+"F0.wireOp",EDGE,"E73.trimOffspring"),sQuery(id+"F0.wireOp",EDGE,"E74.trimOffspring"),sQuery(id+"F0.wireOp",EDGE,"E75.trimOffspring"),sQuery(id+"F0.wireOp",EDGE,"E76.trimOffspring"),sQuery(id+"F0.wireOp",EDGE,"E77.trimOffspring"),sQuery(id+"F0.wireOp",EDGE,"E78.trimOffspring"),sQuery(id+"F0.wireOp",EDGE,"E79.trimOffspring"),sQuery(id+"F0.wireOp",EDGE,"E80.trimOffspring"),sQuery(id+"F0.wireOp",EDGE,"E81.trimOffspring"),sQuery(id+"F0.wireOp",EDGE,"E82.trimOffspring"),sQuery(id+"F0.wireOp",EDGE,"E83"),sQuery(id+"F0.wireOp",EDGE,"E88"),sQuery(id+"F0.wireOp",EDGE,"E89"),sQuery(id+"F0.wireOp",EDGE,"E91"),sQuery(id+"F0.wireOp",EDGE,"E92"),sQuery(id+"F0.wireOp",EDGE,"E93"),sQuery(id+"F0.wireOp",EDGE,"E94"),sQuery(id+"F0.wireOp",EDGE,"E95.trimOffspring"),sQuery(id+"F0.wireOp",EDGE,"E96.trimOffspring"),sQuery(id+"F0.wireOp",EDGE,"E98"),sQuery(id+"F0.wireOp",EDGE,"E99"),sQuery(id+"F0.wireOp",EDGE,"E100"),sQuery(id+"F0.wireOp",EDGE,"E101"),sQuery(id+"F0.wireOp",EDGE,"E102"),sQuery(id+"F0.wireOp",EDGE,"E103"),sQuery(id+"F0.wireOp",EDGE,"E104.trimOffspring"),sQuery(id+"F0.wireOp",EDGE,"E105.trimOffspring")])]});
            hole(context, id + "F5", {"style" : HoleStyle.SIMPLE, "holeDiameter" : 3 * mm, "endStyle" : HoleEndStyle.BLIND, "holeDepth" : 10.4 * mm, "locations" : qUnion([Q0, Q1, Q2, Q3]), "scope" : qUnion([Q4])});
        }
        {
            var Q0;
            Q0=sQuery(id+"F3.wireOp",VERTEX,"E107");
            var Q1;
            Q1=makeQuery(id+"F1.opExtrude","SWEPT_BODY",BODY,{"disambiguationData":[OSD([sQuery(id+"F0.wireOp",EDGE,"E0.rect.top"),sQuery(id+"F0.wireOp",EDGE,"E0.rect.left"),sQuery(id+"F0.wireOp",EDGE,"E0.rect.right"),sQuery(id+"F0.wireOp",EDGE,"E1.rect.left"),sQuery(id+"F0.wireOp",EDGE,"E1.rect.right"),sQuery(id+"F0.wireOp",EDGE,"E2.rect.left"),sQuery(id+"F0.wireOp",EDGE,"E2.rect.right"),sQuery(id+"F0.wireOp",EDGE,"E3.trimOffspring"),sQuery(id+"F0.wireOp",EDGE,"E4.trimOffspring"),sQuery(id+"F0.wireOp",EDGE,"E5.trimOffspring"),sQuery(id+"F0.wireOp",EDGE,"E6.trimOffspring"),sQuery(id+"F0.wireOp",EDGE,"E7.trimOffspring"),sQuery(id+"F0.wireOp",EDGE,"E8.trimOffspring"),sQuery(id+"F0.wireOp",EDGE,"E9.trimOffspring"),sQuery(id+"F0.wireOp",EDGE,"E10.trimOffspring"),sQuery(id+"F0.wireOp",EDGE,"E11.trimOffspring"),sQuery(id+"F0.wireOp",EDGE,"E12.trimOffspring"),sQuery(id+"F0.wireOp",EDGE,"E13.trimOffspring"),sQuery(id+"F0.wireOp",EDGE,"E14.trimOffspring"),sQuery(id+"F0.wireOp",EDGE,"E15.trimOffspring"),sQuery(id+"F0.wireOp",EDGE,"E16.trimOffspring"),sQuery(id+"F0.wireOp",EDGE,"E17.trimOffspring"),sQuery(id+"F0.wireOp",EDGE,"E18.trimOffspring"),sQuery(id+"F0.wireOp",EDGE,"E19.trimOffspring"),sQuery(id+"F0.wireOp",EDGE,"E20.trimOffspring"),sQuery(id+"F0.wireOp",EDGE,"E21.trimOffspring"),sQuery(id+"F0.wireOp",EDGE,"E22.trimOffspring"),sQuery(id+"F0.wireOp",EDGE,"E23.trimOffspring"),sQuery(id+"F0.wireOp",EDGE,"E24.trimOffspring"),sQuery(id+"F0.wireOp",EDGE,"E25.trimOffspring"),sQuery(id+"F0.wireOp",EDGE,"E26.trimOffspring"),sQuery(id+"F0.wireOp",EDGE,"E29.rect.bottom"),sQuery(id+"F0.wireOp",EDGE,"E29.rect.top"),sQuery(id+"F0.wireOp",EDGE,"E30.rect.bottom"),sQuery(id+"F0.wireOp",EDGE,"E30.rect.top"),sQuery(id+"F0.wireOp",EDGE,"E31.rect.bottom"),sQuery(id+"F0.wireOp",EDGE,"E31.rect.top"),sQuery(id+"F0.wireOp",EDGE,"E32.rect.left"),sQuery(id+"F0.wireOp",EDGE,"E33.trimOffspring"),sQuery(id+"F0.wireOp",EDGE,"E34.trimOffspring"),sQuery(id+"F0.wireOp",EDGE,"E35.trimOffspring"),sQuery(id+"F0.wireOp",EDGE,"E36.trimOffspring"),sQuery(id+"F0.wireOp",EDGE,"E37.trimOffspring"),sQuery(id+"F0.wireOp",EDGE,"E38.trimOffspring"),sQuery(id+"F0.wireOp",EDGE,"E39.trimOffspring"),sQuery(id+"F0.wireOp",EDGE,"E40.trimOffspring"),sQuery(id+"F0.wireOp",EDGE,"E41.trimOffspring"),sQuery(id+"F0.wireOp",EDGE,"E42.trimOffspring"),sQuery(id+"F0.wireOp",EDGE,"E43.trimOffspring"),sQuery(id+"F0.wireOp",EDGE,"E44.trimOffspring"),sQuery(id+"F0.wireOp",EDGE,"E45.trimOffspring"),sQuery(id+"F0.wireOp",EDGE,"E46.trimOffspring"),sQuery(id+"F0.wireOp",EDGE,"E47.trimOffspring"),sQuery(id+"F0.wireOp",EDGE,"E48.trimOffspring"),sQuery(id+"F0.wireOp",EDGE,"E49.trimOffspring"),sQuery(id+"F0.wireOp",EDGE,"E50.trimOffspring"),sQuery(id+"F0.wireOp",EDGE,"E51.trimOffspring"),sQuery(id+"F0.wireOp",EDGE,"E52.trimOffspring"),sQuery(id+"F0.wireOp",EDGE,"E53.trimOffspring"),sQuery(id+"F0.wireOp",EDGE,"E54.trimOffspring"),sQuery(id+"F0.wireOp",EDGE,"E56.trimOffspring"),sQuery(id+"F0.wireOp",EDGE,"E57.trimOffspring"),sQuery(id+"F0.wireOp",EDGE,"E58.trimOffspring"),sQuery(id+"F0.wireOp",EDGE,"E59.trimOffspring"),sQuery(id+"F0.wireOp",EDGE,"E60.trimOffspring"),sQuery(id+"F0.wireOp",EDGE,"E61.trimOffspring"),sQuery(id+"F0.wireOp",EDGE,"E62.trimOffspring"),sQuery(id+"F0.wireOp",EDGE,"E63.trimOffspring"),sQuery(id+"F0.wireOp",EDGE,"E64.trimOffspring"),sQuery(id+"F0.wireOp",EDGE,"E65.trimOffspring"),sQuery(id+"F0.wireOp",EDGE,"E66.trimOffspring"),sQuery(id+"F0.wireOp",EDGE,"E67.trimOffspring"),sQuery(id+"F0.wireOp",EDGE,"E68.trimOffspring"),sQuery(id+"F0.wireOp",EDGE,"E69.trimOffspring"),sQuery(id+"F0.wireOp",EDGE,"E70"),sQuery(id+"F0.wireOp",EDGE,"E71.trimOffspring"),sQuery(id+"F0.wireOp",EDGE,"E72.trimOffspring"),sQuery(id+"F0.wireOp",EDGE,"E73.trimOffspring"),sQuery(id+"F0.wireOp",EDGE,"E74.trimOffspring"),sQuery(id+"F0.wireOp",EDGE,"E75.trimOffspring"),sQuery(id+"F0.wireOp",EDGE,"E76.trimOffspring"),sQuery(id+"F0.wireOp",EDGE,"E77.trimOffspring"),sQuery(id+"F0.wireOp",EDGE,"E78.trimOffspring"),sQuery(id+"F0.wireOp",EDGE,"E79.trimOffspring"),sQuery(id+"F0.wireOp",EDGE,"E80.trimOffspring"),sQuery(id+"F0.wireOp",EDGE,"E81.trimOffspring"),sQuery(id+"F0.wireOp",EDGE,"E82.trimOffspring"),sQuery(id+"F0.wireOp",EDGE,"E83"),sQuery(id+"F0.wireOp",EDGE,"E88"),sQuery(id+"F0.wireOp",EDGE,"E89"),sQuery(id+"F0.wireOp",EDGE,"E91"),sQuery(id+"F0.wireOp",EDGE,"E92"),sQuery(id+"F0.wireOp",EDGE,"E93"),sQuery(id+"F0.wireOp",EDGE,"E94"),sQuery(id+"F0.wireOp",EDGE,"E95.trimOffspring"),sQuery(id+"F0.wireOp",EDGE,"E96.trimOffspring"),sQuery(id+"F0.wireOp",EDGE,"E98"),sQuery(id+"F0.wireOp",EDGE,"E99"),sQuery(id+"F0.wireOp",EDGE,"E100"),sQuery(id+"F0.wireOp",EDGE,"E101"),sQuery(id+"F0.wireOp",EDGE,"E102"),sQuery(id+"F0.wireOp",EDGE,"E103"),sQuery(id+"F0.wireOp",EDGE,"E104.trimOffspring"),sQuery(id+"F0.wireOp",EDGE,"E105.trimOffspring")])]});
            hole(context, id + "F6", {"style" : HoleStyle.SIMPLE, "holeDiameter" : 5.33 * mm, "endStyle" : HoleEndStyle.BLIND, "holeDepth" : 7.87 * mm, "locations" : qUnion([Q0]), "scope" : qUnion([Q1])});
        }
        {
            var Q0;
            Q0=sQuery(id+"F3.wireOp",VERTEX,"E113");
            var Q1;
            Q1=sQuery(id+"F3.wireOp",VERTEX,"E114");
            var Q2;
            Q2=sQuery(id+"F3.wireOp",VERTEX,"E109");
            var Q3;
            Q3=sQuery(id+"F3.wireOp",VERTEX,"E110");
            var Q4;
            Q4=sQuery(id+"F3.wireOp",VERTEX,"E111");
            var Q5;
            Q5=sQuery(id+"F3.wireOp",VERTEX,"E112");
            var Q6;
            Q6=sQuery(id+"F3.wireOp",VERTEX,"E107");
            var Q7;
            Q7=makeQuery(id+"F1.opExtrude","SWEPT_BODY",BODY,{"disambiguationData":[OSD([sQuery(id+"F0.wireOp",EDGE,"E0.rect.top"),sQuery(id+"F0.wireOp",EDGE,"E0.rect.left"),sQuery(id+"F0.wireOp",EDGE,"E0.rect.right"),sQuery(id+"F0.wireOp",EDGE,"E1.rect.left"),sQuery(id+"F0.wireOp",EDGE,"E1.rect.right"),sQuery(id+"F0.wireOp",EDGE,"E2.rect.left"),sQuery(id+"F0.wireOp",EDGE,"E2.rect.right"),sQuery(id+"F0.wireOp",EDGE,"E3.trimOffspring"),sQuery(id+"F0.wireOp",EDGE,"E4.trimOffspring"),sQuery(id+"F0.wireOp",EDGE,"E5.trimOffspring"),sQuery(id+"F0.wireOp",EDGE,"E6.trimOffspring"),sQuery(id+"F0.wireOp",EDGE,"E7.trimOffspring"),sQuery(id+"F0.wireOp",EDGE,"E8.trimOffspring"),sQuery(id+"F0.wireOp",EDGE,"E9.trimOffspring"),sQuery(id+"F0.wireOp",EDGE,"E10.trimOffspring"),sQuery(id+"F0.wireOp",EDGE,"E11.trimOffspring"),sQuery(id+"F0.wireOp",EDGE,"E12.trimOffspring"),sQuery(id+"F0.wireOp",EDGE,"E13.trimOffspring"),sQuery(id+"F0.wireOp",EDGE,"E14.trimOffspring"),sQuery(id+"F0.wireOp",EDGE,"E15.trimOffspring"),sQuery(id+"F0.wireOp",EDGE,"E16.trimOffspring"),sQuery(id+"F0.wireOp",EDGE,"E17.trimOffspring"),sQuery(id+"F0.wireOp",EDGE,"E18.trimOffspring"),sQuery(id+"F0.wireOp",EDGE,"E19.trimOffspring"),sQuery(id+"F0.wireOp",EDGE,"E20.trimOffspring"),sQuery(id+"F0.wireOp",EDGE,"E21.trimOffspring"),sQuery(id+"F0.wireOp",EDGE,"E22.trimOffspring"),sQuery(id+"F0.wireOp",EDGE,"E23.trimOffspring"),sQuery(id+"F0.wireOp",EDGE,"E24.trimOffspring"),sQuery(id+"F0.wireOp",EDGE,"E25.trimOffspring"),sQuery(id+"F0.wireOp",EDGE,"E26.trimOffspring"),sQuery(id+"F0.wireOp",EDGE,"E29.rect.bottom"),sQuery(id+"F0.wireOp",EDGE,"E29.rect.top"),sQuery(id+"F0.wireOp",EDGE,"E30.rect.bottom"),sQuery(id+"F0.wireOp",EDGE,"E30.rect.top"),sQuery(id+"F0.wireOp",EDGE,"E31.rect.bottom"),sQuery(id+"F0.wireOp",EDGE,"E31.rect.top"),sQuery(id+"F0.wireOp",EDGE,"E32.rect.left"),sQuery(id+"F0.wireOp",EDGE,"E33.trimOffspring"),sQuery(id+"F0.wireOp",EDGE,"E34.trimOffspring"),sQuery(id+"F0.wireOp",EDGE,"E35.trimOffspring"),sQuery(id+"F0.wireOp",EDGE,"E36.trimOffspring"),sQuery(id+"F0.wireOp",EDGE,"E37.trimOffspring"),sQuery(id+"F0.wireOp",EDGE,"E38.trimOffspring"),sQuery(id+"F0.wireOp",EDGE,"E39.trimOffspring"),sQuery(id+"F0.wireOp",EDGE,"E40.trimOffspring"),sQuery(id+"F0.wireOp",EDGE,"E41.trimOffspring"),sQuery(id+"F0.wireOp",EDGE,"E42.trimOffspring"),sQuery(id+"F0.wireOp",EDGE,"E43.trimOffspring"),sQuery(id+"F0.wireOp",EDGE,"E44.trimOffspring"),sQuery(id+"F0.wireOp",EDGE,"E45.trimOffspring"),sQuery(id+"F0.wireOp",EDGE,"E46.trimOffspring"),sQuery(id+"F0.wireOp",EDGE,"E47.trimOffspring"),sQuery(id+"F0.wireOp",EDGE,"E48.trimOffspring"),sQuery(id+"F0.wireOp",EDGE,"E49.trimOffspring"),sQuery(id+"F0.wireOp",EDGE,"E50.trimOffspring"),sQuery(id+"F0.wireOp",EDGE,"E51.trimOffspring"),sQuery(id+"F0.wireOp",EDGE,"E52.trimOffspring"),sQuery(id+"F0.wireOp",EDGE,"E53.trimOffspring"),sQuery(id+"F0.wireOp",EDGE,"E54.trimOffspring"),sQuery(id+"F0.wireOp",EDGE,"E56.trimOffspring"),sQuery(id+"F0.wireOp",EDGE,"E57.trimOffspring"),sQuery(id+"F0.wireOp",EDGE,"E58.trimOffspring"),sQuery(id+"F0.wireOp",EDGE,"E59.trimOffspring"),sQuery(id+"F0.wireOp",EDGE,"E60.trimOffspring"),sQuery(id+"F0.wireOp",EDGE,"E61.trimOffspring"),sQuery(id+"F0.wireOp",EDGE,"E62.trimOffspring"),sQuery(id+"F0.wireOp",EDGE,"E63.trimOffspring"),sQuery(id+"F0.wireOp",EDGE,"E64.trimOffspring"),sQuery(id+"F0.wireOp",EDGE,"E65.trimOffspring"),sQuery(id+"F0.wireOp",EDGE,"E66.trimOffspring"),sQuery(id+"F0.wireOp",EDGE,"E67.trimOffspring"),sQuery(id+"F0.wireOp",EDGE,"E68.trimOffspring"),sQuery(id+"F0.wireOp",EDGE,"E69.trimOffspring"),sQuery(id+"F0.wireOp",EDGE,"E70"),sQuery(id+"F0.wireOp",EDGE,"E71.trimOffspring"),sQuery(id+"F0.wireOp",EDGE,"E72.trimOffspring"),sQuery(id+"F0.wireOp",EDGE,"E73.trimOffspring"),sQuery(id+"F0.wireOp",EDGE,"E74.trimOffspring"),sQuery(id+"F0.wireOp",EDGE,"E75.trimOffspring"),sQuery(id+"F0.wireOp",EDGE,"E76.trimOffspring"),sQuery(id+"F0.wireOp",EDGE,"E77.trimOffspring"),sQuery(id+"F0.wireOp",EDGE,"E78.trimOffspring"),sQuery(id+"F0.wireOp",EDGE,"E79.trimOffspring"),sQuery(id+"F0.wireOp",EDGE,"E80.trimOffspring"),sQuery(id+"F0.wireOp",EDGE,"E81.trimOffspring"),sQuery(id+"F0.wireOp",EDGE,"E82.trimOffspring"),sQuery(id+"F0.wireOp",EDGE,"E83"),sQuery(id+"F0.wireOp",EDGE,"E88"),sQuery(id+"F0.wireOp",EDGE,"E89"),sQuery(id+"F0.wireOp",EDGE,"E91"),sQuery(id+"F0.wireOp",EDGE,"E92"),sQuery(id+"F0.wireOp",EDGE,"E93"),sQuery(id+"F0.wireOp",EDGE,"E94"),sQuery(id+"F0.wireOp",EDGE,"E95.trimOffspring"),sQuery(id+"F0.wireOp",EDGE,"E96.trimOffspring"),sQuery(id+"F0.wireOp",EDGE,"E98"),sQuery(id+"F0.wireOp",EDGE,"E99"),sQuery(id+"F0.wireOp",EDGE,"E100"),sQuery(id+"F0.wireOp",EDGE,"E101"),sQuery(id+"F0.wireOp",EDGE,"E102"),sQuery(id+"F0.wireOp",EDGE,"E103"),sQuery(id+"F0.wireOp",EDGE,"E104.trimOffspring"),sQuery(id+"F0.wireOp",EDGE,"E105.trimOffspring")])]});
            hole(context, id + "F7", {"style" : HoleStyle.SIMPLE, "holeDiameter" : 5.6 * mm, "endStyle" : HoleEndStyle.BLIND, "holeDepth" : 10.4 * mm, "locations" : qUnion([Q0, Q1, Q2, Q3, Q4, Q5, Q6]), "scope" : qUnion([Q7])});
        }
    });
